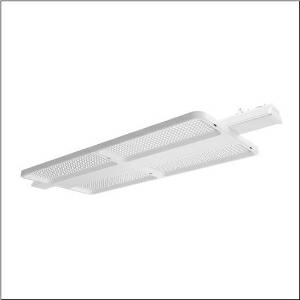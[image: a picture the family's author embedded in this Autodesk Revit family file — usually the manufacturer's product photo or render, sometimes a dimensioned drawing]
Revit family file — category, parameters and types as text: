
# Revit family: highbay_11_fur_licross_tragschiene_maxi_51hn11db4qla
name_source: partatom
category: Lighting Fixtures
units: mm (PartAtom-declared; Revit-internal decimal feet)

## family parameters
Cut with Voids When Loaded = No
Host = Face
Light Source = No
Part Type = Normal
Room Calculation Point = No
Round Connector Dimension = Use Diameter
Shared = No

## types (1)
- --- (1 x LED, 36000 lm, 177.7 W, 4000K)
    Apparent Load = 178 VA
    CIE Flux Codes = 85 97 100 100 100
    Color Rendering = 80
    Color Temperature = 4000K
    Default Elevation = 1800 mm
    Description = high bay luminaire Highbay 11 for Licross trunking rail maxi; direct symmetric narrow distribution, light control with lens of PMMA; UGR ≤ 22 (X = 4H | Y = 8H | S = 0.25H | reflection values 70/50/20); luminous flux: 36.000lm; light colour: 840, colour temperature: 4000K, MacAdam ≤ 2 SDCM (initial), colour rendering: CRI > 80; luminous efficacy: 202,6lm/W; rated service life: 100.000h (L95) at AT= 25°C; control: DALI 2; luminaire connection: plug, 5-pole, with phase selectionmains connection: 230..240V, AC 50/60Hz; connected load: 177,7W; protection rating (complete): IP64; insulation class (complete): insulation class I (protective earthing); protection symbol: D; impact resistance: IK06; certification: CE, ENEC, VDE, UKCA; internal wiring halogen-free; luminaire LABS conformity tested according to VDMA 24364:2018-05; Suitable for use in the food industry according to the specifications of IFS-Food, HACCP and/or BRC; housing frame of high-performance plastic PA6, matt traffic white (RAL 9016); cover of PMMA; fixing on rail side of steel, galvanised, white; blank cover of PC/ABS, traffic white (RAL 9016); dimension (LxWxH): 1.250 x 442 x 71mm; permissible operating ambient temperature: -40..+55°C (reducing of maximum allowable ambient temperature of 5°C with ceiling mounting); packaging unit: 1 piece
    Height = 72 mm  [stored 0.23622 ft]
    Lamp = 1 x LED
    Lamp Light Flux = 36000 lm
    Lamp Power = 177.7 W
    Lamp count = 1
    Length = 946 mm
    Luminous efficacy = 203 lm/W
    Manufacturer = Siteco
    ModVariant = No
    Model = 51HN11DB4QLA
    Mounting Place = Ceiling
    Mounting Type = Pendant
    Number of Poles = 1
    OnlyDefault = Yes
    Power Factor = 1
    Product Name = Highbay 11 für Licross Tragschiene maxi
    Product group = high bay luminaire
    ProductGroupID = 902
    Protection Class = Protection class I
    Protection Degree = IP 64
    RLX_Detail_Level = 1
    RLX_Emergency_Light_Flux = 0 lm
    RLX_Emergency_Type = 0
    RLX_Emergency_Type_DB = No
    RlxData = <blob elided: 24289 chars, md5=0d256ead>
    Socket = socket
    Standby Power = 0 W
    System Light Flux = 36000 lm
    System Power = 178 W
    Type Comments = factory setting: luminous flux: 100 % | dim-lin: 254 | 824 mA
    Type Image = l_1361711.jpg
    URL = http://relux.com
    VarID = @adj_024411
    Voltage = 0 V
    Weight = 0.00 kg
    Width = 442 mm

note: [stored X ft] marks values corroborated as IEEE doubles in the binary element streams (Revit-internal decimal feet)

## geometry (parser evidence)
native form markers: Blend x4, Sweep x11
no freeform markers — native parametric forms only
